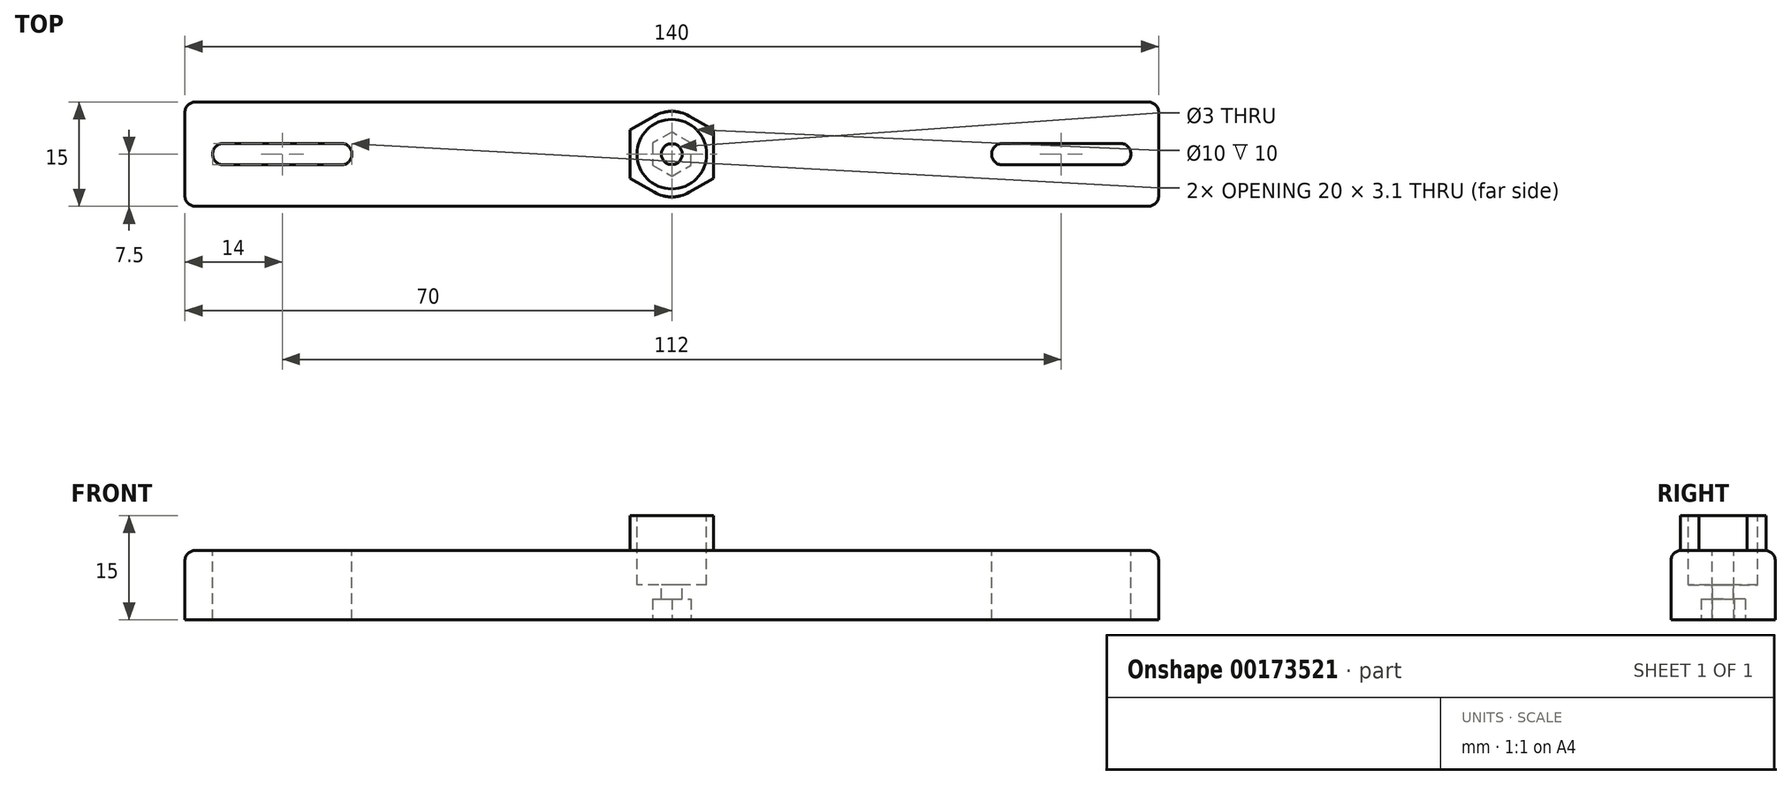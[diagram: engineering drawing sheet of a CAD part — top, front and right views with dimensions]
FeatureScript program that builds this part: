
annotation { "Feature Type Name" : "Feature", "Feature Type Description" : "" }
export const myFeature = defineFeature(function(context is Context, id is Id, definition is map)
    precondition{}
    {
        {
            var Q0;
            Q0=qCreatedBy(makeId("Top.planeOp"),FACE);
            var sketch = newSketch(context, id + "F0", { "sketchPlane" : qUnion([Q0])});
            skLineSegment(sketch, "E0.bottom", {"start": v(70, 7.5) * mm, "end": v(-70, 7.5) * mm});
            skLineSegment(sketch, "E0.top", {"start": v(70, -7.5) * mm, "end": v(-70, -7.5) * mm});
            skLineSegment(sketch, "E0.left", {"start": v(70, 7.5) * mm, "end": v(70, -7.5) * mm});
            skLineSegment(sketch, "E0.right", {"start": v(-70, 7.5) * mm, "end": v(-70, -7.5) * mm});
            skPoint(sketch, "E0.middle", {"position": v(0, 0) * mm});
            skSolve(sketch);
        }
        {
            var Q0;
            Q0=makeQuery(id+"F0.imprint","IMPRINT",FACE,{"disambiguationData":[TD([[makeQuery(id+"F0.imprint","IMPRINT",EDGE,{"derivedFrom":sQuery(id+"F0.wireOp",EDGE,"E0.bottom")}),1.0]])]});
            extrude(context, id + "F1", {"entities" : qUnion([Q0]), "depth" : 10 * mm});
        }
        {
            var Q0;
            Q0=makeQuery(id+"F1.opExtrude","CAP_FACE",FACE,{"disambiguationData":[OSD([sQuery(id+"F0.wireOp",EDGE,"E0.bottom"),sQuery(id+"F0.wireOp",EDGE,"E0.top"),sQuery(id+"F0.wireOp",EDGE,"E0.left"),sQuery(id+"F0.wireOp",EDGE,"E0.right")])],"isStart":false});
            var sketch = newSketch(context, id + "F2", { "sketchPlane" : qUnion([Q0])});
            skLineSegment(sketch, "E1.bottom", {"start": v(-46, 1.55) * mm, "end": v(-66, 1.55) * mm});
            skLineSegment(sketch, "E1.top", {"start": v(-46, -1.55) * mm, "end": v(-66, -1.55) * mm});
            skLineSegment(sketch, "E1.left", {"start": v(-46, 1.55) * mm, "end": v(-46, -1.55) * mm});
            skLineSegment(sketch, "E1.right", {"start": v(-66, 1.55) * mm, "end": v(-66, -1.55) * mm});
            skPoint(sketch, "E1.middle", {"position": v(-56, 0) * mm});
            skLineSegment(sketch, "E2.bottom", {"start": v(66, 1.55) * mm, "end": v(46, 1.55) * mm});
            skLineSegment(sketch, "E2.top", {"start": v(66, -1.55) * mm, "end": v(46, -1.55) * mm});
            skLineSegment(sketch, "E2.left", {"start": v(66, 1.55) * mm, "end": v(66, -1.55) * mm});
            skLineSegment(sketch, "E2.right", {"start": v(46, 1.55) * mm, "end": v(46, -1.55) * mm});
            skPoint(sketch, "E2.middle", {"position": v(56, 0) * mm});
            skSolve(sketch);
        }
        {
            var Q0;
            Q0 = qSketchRegion(id + "F2", true);
            extrude(context, id + "F3", {"entities" : qUnion([Q0]), "operationType" : NewBodyOperationType.REMOVE, "oppositeDirection" : true, "depth" : 25 * mm, "hasSecondDirection" : true, "secondDirectionOppositeDirection" : false, "secondDirectionDepth" : 25 * mm});
        }
        {
            var Q0;
            Q0=makeQuery(id+"F1.opExtrude","CAP_FACE",FACE,{"disambiguationData":[OSD([sQuery(id+"F0.wireOp",EDGE,"E0.bottom"),sQuery(id+"F0.wireOp",EDGE,"E0.top"),sQuery(id+"F0.wireOp",EDGE,"E0.left"),sQuery(id+"F0.wireOp",EDGE,"E0.right")])],"isStart":false});
            var sketch = newSketch(context, id + "F4", { "sketchPlane" : qUnion([Q0])});
            skCircle(sketch, "E3.cCircle", {"center": v(0, 0) * mm, "radius": 6 * mm, "construction": true});
            skLineSegment(sketch, "E3.0", {"start": v(6, 3.46) * mm, "end": v(6, -3.46) * mm});
            skLineSegment(sketch, "E3.1", {"start": v(6, -3.46) * mm, "end": v(0, -6.93) * mm});
            skLineSegment(sketch, "E3.2", {"start": v(0, -6.93) * mm, "end": v(-6, -3.46) * mm});
            skLineSegment(sketch, "E3.3", {"start": v(-6, -3.46) * mm, "end": v(-6, 3.46) * mm});
            skLineSegment(sketch, "E3.4", {"start": v(-6, 3.46) * mm, "end": v(0, 6.93) * mm});
            skLineSegment(sketch, "E3.5", {"start": v(0, 6.93) * mm, "end": v(6, 3.46) * mm});
            skPoint(sketch, "E3.0.midPoint", {"position": v(6, 0) * mm});
            skSolve(sketch);
        }
        {
            var Q0;
            Q0 = qSketchRegion(id + "F4", true);
            extrude(context, id + "F5", {"entities" : qUnion([Q0]), "operationType" : NewBodyOperationType.ADD, "depth" : 5 * mm});
        }
        {
            var Q0;
            Q0=makeQuery(id+"F5.opExtrude","CAP_FACE",FACE,{"disambiguationData":[OSD([sQuery(id+"F4.wireOp",EDGE,"E3.0"),sQuery(id+"F4.wireOp",EDGE,"E3.1"),sQuery(id+"F4.wireOp",EDGE,"E3.2"),sQuery(id+"F4.wireOp",EDGE,"E3.3"),sQuery(id+"F4.wireOp",EDGE,"E3.4"),sQuery(id+"F4.wireOp",EDGE,"E3.5")])],"isStart":false});
            var sketch = newSketch(context, id + "F6", { "sketchPlane" : qUnion([Q0])});
            skCircle(sketch, "E4", {"center": v(0, 0) * mm, "radius": 5 * mm});
            skSolve(sketch);
        }
        {
            var Q0;
            Q0 = qSketchRegion(id + "F6", true);
            extrude(context, id + "F7", {"entities" : qUnion([Q0]), "operationType" : NewBodyOperationType.REMOVE, "oppositeDirection" : true, "depth" : 10 * mm});
        }
        {
            var Q0;
            Q0=makeQuery(id+"F7.boolean.opBoolean","COPY",FACE,{"derivedFrom":makeQuery(id+"F7.opExtrude","CAP_FACE",FACE,{"disambiguationData":[OSD([sQuery(id+"F6.wireOp",EDGE,"E4")])],"isStart":false})});
            var sketch = newSketch(context, id + "F8", { "sketchPlane" : qUnion([Q0])});
            skCircle(sketch, "E5", {"center": v(0, 0) * mm, "radius": 1.5 * mm});
            skSolve(sketch);
        }
        {
            var Q0;
            Q0 = qSketchRegion(id + "F8", true);
            extrude(context, id + "F9", {"entities" : qUnion([Q0]), "operationType" : NewBodyOperationType.REMOVE, "oppositeDirection" : true, "depth" : 25 * mm, "hasSecondDirection" : true, "secondDirectionOppositeDirection" : false, "secondDirectionDepth" : 25 * mm});
        }
        {
            var Q0;
            Q0=makeQuery(id+"F1.opExtrude","CAP_FACE",FACE,{"disambiguationData":[OSD([sQuery(id+"F0.wireOp",EDGE,"E0.bottom"),sQuery(id+"F0.wireOp",EDGE,"E0.top"),sQuery(id+"F0.wireOp",EDGE,"E0.left"),sQuery(id+"F0.wireOp",EDGE,"E0.right")])],"isStart":true});
            var sketch = newSketch(context, id + "F10", { "sketchPlane" : qUnion([Q0])});
            skCircle(sketch, "E6.cCircle", {"center": v(0, 0) * mm, "radius": 2.75 * mm, "construction": true});
            skLineSegment(sketch, "E6.0", {"start": v(2.75, 1.59) * mm, "end": v(2.75, -1.59) * mm});
            skLineSegment(sketch, "E6.1", {"start": v(2.75, -1.59) * mm, "end": v(0, -3.18) * mm});
            skLineSegment(sketch, "E6.2", {"start": v(0, -3.18) * mm, "end": v(-2.75, -1.59) * mm});
            skLineSegment(sketch, "E6.3", {"start": v(-2.75, -1.59) * mm, "end": v(-2.75, 1.59) * mm});
            skLineSegment(sketch, "E6.4", {"start": v(-2.75, 1.59) * mm, "end": v(0, 3.18) * mm});
            skLineSegment(sketch, "E6.5", {"start": v(0, 3.18) * mm, "end": v(2.75, 1.59) * mm});
            skPoint(sketch, "E6.0.midPoint", {"position": v(2.75, 0) * mm});
            skSolve(sketch);
        }
        {
            var Q0;
            Q0 = qSketchRegion(id + "F10", true);
            extrude(context, id + "F11", {"entities" : qUnion([Q0]), "operationType" : NewBodyOperationType.REMOVE, "oppositeDirection" : true, "depth" : 3 * mm});
        }
        {
            var Q0;
            Q0=makeQuery(id+"F3.boolean.opBoolean","COPY",EDGE,{"derivedFrom":makeQuery(id+"F3.opExtrude","SWEPT_EDGE",EDGE,{"disambiguationData":[OSD([sQuery(id+"F2.wireOp",EDGE,"E1.bottom"),sQuery(id+"F2.wireOp",EDGE,"E1.right")])]})});
            var Q1;
            Q1=makeQuery(id+"F3.boolean.opBoolean","COPY",EDGE,{"derivedFrom":makeQuery(id+"F3.opExtrude","SWEPT_EDGE",EDGE,{"disambiguationData":[OSD([sQuery(id+"F2.wireOp",EDGE,"E1.top"),sQuery(id+"F2.wireOp",EDGE,"E1.right")])]})});
            var Q2;
            Q2=makeQuery(id+"F3.boolean.opBoolean","COPY",EDGE,{"derivedFrom":makeQuery(id+"F3.opExtrude","SWEPT_EDGE",EDGE,{"disambiguationData":[OSD([sQuery(id+"F2.wireOp",EDGE,"E1.bottom"),sQuery(id+"F2.wireOp",EDGE,"E1.left")])]})});
            var Q3;
            Q3=makeQuery(id+"F3.boolean.opBoolean","COPY",EDGE,{"derivedFrom":makeQuery(id+"F3.opExtrude","SWEPT_EDGE",EDGE,{"disambiguationData":[OSD([sQuery(id+"F2.wireOp",EDGE,"E1.top"),sQuery(id+"F2.wireOp",EDGE,"E1.left")])]})});
            var Q4;
            Q4=makeQuery(id+"F3.boolean.opBoolean","COPY",EDGE,{"derivedFrom":makeQuery(id+"F3.opExtrude","SWEPT_EDGE",EDGE,{"disambiguationData":[OSD([sQuery(id+"F2.wireOp",EDGE,"E2.bottom"),sQuery(id+"F2.wireOp",EDGE,"E2.left")])]})});
            var Q5;
            Q5=makeQuery(id+"F3.boolean.opBoolean","COPY",EDGE,{"derivedFrom":makeQuery(id+"F3.opExtrude","SWEPT_EDGE",EDGE,{"disambiguationData":[OSD([sQuery(id+"F2.wireOp",EDGE,"E2.bottom"),sQuery(id+"F2.wireOp",EDGE,"E2.right")])]})});
            var Q6;
            Q6=makeQuery(id+"F3.boolean.opBoolean","COPY",EDGE,{"derivedFrom":makeQuery(id+"F3.opExtrude","SWEPT_EDGE",EDGE,{"disambiguationData":[OSD([sQuery(id+"F2.wireOp",EDGE,"E2.top"),sQuery(id+"F2.wireOp",EDGE,"E2.left")])]})});
            var Q7;
            Q7=makeQuery(id+"F3.boolean.opBoolean","COPY",EDGE,{"derivedFrom":makeQuery(id+"F3.opExtrude","SWEPT_EDGE",EDGE,{"disambiguationData":[OSD([sQuery(id+"F2.wireOp",EDGE,"E2.top"),sQuery(id+"F2.wireOp",EDGE,"E2.right")])]})});
            var Q8;
            Q8=makeQuery(id+"F1.opExtrude","SWEPT_EDGE",EDGE,{"disambiguationData":[OSD([sQuery(id+"F0.wireOp",EDGE,"E0.bottom"),sQuery(id+"F0.wireOp",EDGE,"E0.left")])]});
            var Q9;
            Q9=makeQuery(id+"F1.opExtrude","SWEPT_EDGE",EDGE,{"disambiguationData":[OSD([sQuery(id+"F0.wireOp",EDGE,"E0.top"),sQuery(id+"F0.wireOp",EDGE,"E0.left")])]});
            var Q10;
            Q10=makeQuery(id+"F1.opExtrude","SWEPT_EDGE",EDGE,{"disambiguationData":[OSD([sQuery(id+"F0.wireOp",EDGE,"E0.top"),sQuery(id+"F0.wireOp",EDGE,"E0.right")])]});
            var Q11;
            Q11=makeQuery(id+"F1.opExtrude","SWEPT_EDGE",EDGE,{"disambiguationData":[OSD([sQuery(id+"F0.wireOp",EDGE,"E0.bottom"),sQuery(id+"F0.wireOp",EDGE,"E0.right")])]});
            var Q12;
            Q12=makeQuery(id+"F1.opExtrude","CAP_EDGE",EDGE,{"disambiguationData":[OSD([sQuery(id+"F0.wireOp",EDGE,"E0.top")])],"isStart":false});
            var Q13;
            Q13=makeQuery(id+"F1.opExtrude","CAP_EDGE",EDGE,{"disambiguationData":[OSD([sQuery(id+"F0.wireOp",EDGE,"E0.bottom")])],"isStart":false});
            var Q14;
            Q14=makeQuery(id+"F1.opExtrude","CAP_EDGE",EDGE,{"disambiguationData":[OSD([sQuery(id+"F0.wireOp",EDGE,"E0.right")])],"isStart":false});
            var Q15;
            Q15=makeQuery(id+"F1.opExtrude","CAP_EDGE",EDGE,{"disambiguationData":[OSD([sQuery(id+"F0.wireOp",EDGE,"E0.left")])],"isStart":false});
            fillet(context, id + "F12", {"entities" : qUnion([Q0, Q1, Q2, Q3, Q4, Q5, Q6, Q7, Q8, Q9, Q10, Q11, Q12, Q13, Q14, Q15]), "radius" : 1.5 * mm, "tangentPropagation" : true, "allowEdgeOverflow" : false});
        }
        {
            var Q0;
            Q0=makeQuery(id+"F5.opExtrude","SWEPT_EDGE",EDGE,{"disambiguationData":[OSD([sQuery(id+"F4.wireOp",EDGE,"E3.1"),sQuery(id+"F4.wireOp",EDGE,"E3.2")])]});
            var Q1;
            Q1=makeQuery(id+"F5.opExtrude","SWEPT_EDGE",EDGE,{"disambiguationData":[OSD([sQuery(id+"F4.wireOp",EDGE,"E3.4"),sQuery(id+"F4.wireOp",EDGE,"E3.5")])]});
            fillet(context, id + "F13", {"entities" : qUnion([Q0, Q1]), "radius" : 5 * mm, "tangentPropagation" : true, "allowEdgeOverflow" : false});
        }
    });
